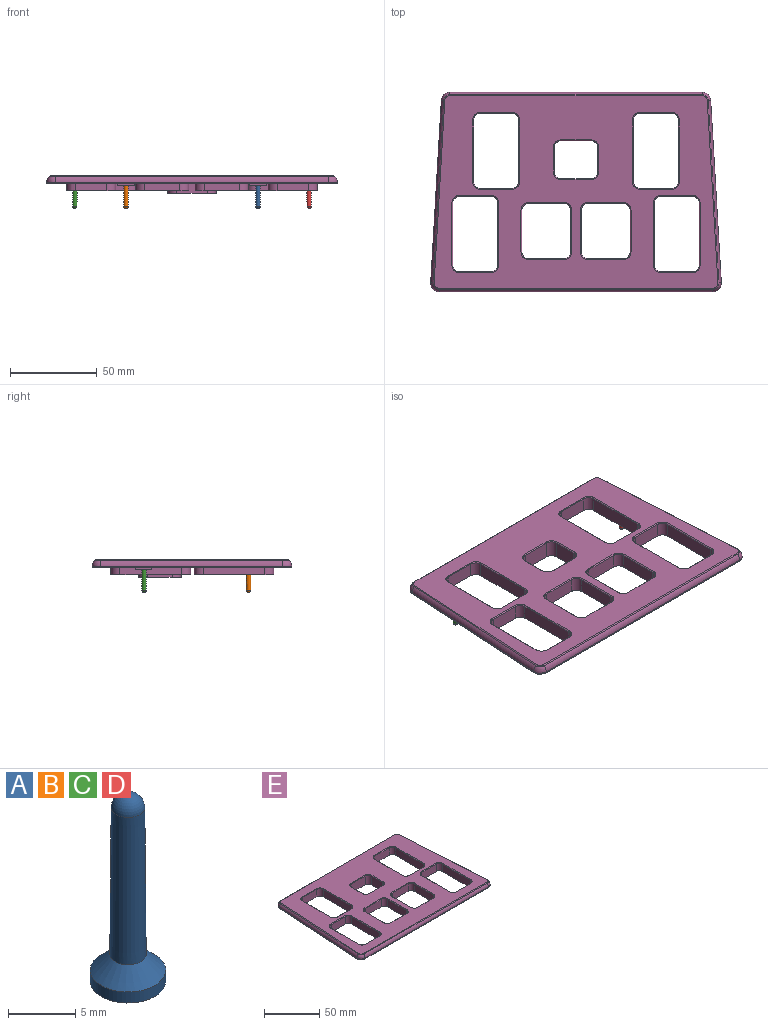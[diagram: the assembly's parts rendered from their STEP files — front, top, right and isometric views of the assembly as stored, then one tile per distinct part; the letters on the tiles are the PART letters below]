
ASSEMBLY  parts=5 mates=4
PART A: 5 faces, bbox 5.6x5.6x17 mm
  f0: plane 5.6x5.6mm, normal (0,0,-1), area 24.6mm2, adj f4
  f1: sphere r=1.25mm, area 9.7mm2, adj f2
  f2: cone r=1.35mm half-angle=0.4deg, axis (0,0,-1), area 108.7mm2, adj f1,f3
  f3: cone r=2.8mm half-angle=45deg, axis (0,0,-1), area 26.7mm2, adj f2,f4
  f4: cylinder r=2.8mm len=5.6mm, axis (0,0,-1), area 17.6mm2, adj f0,f3
PART B: same geometry as A
PART C: same geometry as A
PART D: same geometry as A
PART E: 302 faces, bbox 167.4x115x10.2 mm
  f0: plane 5.45x1.2mm, normal (-1,0,0), area 3.9mm2, adj f7,f10,f181,f219,f299,f301
  f1: plane 5.45x1.2mm, normal (1,0,0), area 3.9mm2, adj f7,f8,f181,f215,f297,f298
  f2: plane 5.45x1.2mm, normal (1,0,0), area 3.9mm2, adj f183,f184,f189,f210,f294,f295
  f3: plane 5.45x1.2mm, normal (1,0,0), area 3.9mm2, adj f176,f177,f178,f191,f287,f289
  f4: plane 5.45x1.2mm, normal (-1,0,0), area 3.9mm2, adj f12,f13,f170,f198,f282,f283
  f5: plane 5.45x1.2mm, normal (1,0,0), area 3.9mm2, adj f11,f12,f170,f203,f278,f280
  f6: plane 162.6x110.2mm, normal (0,0,-1), area 8755.4mm2, adj f8,f9,f10,f11,f13,f80,f81,f82
  f7: plane 2.9x1.2mm, normal (0,1,0), area 3.5mm2, adj f0,f1,f181,f214
  f8: plane 3.9x2.6mm, normal (0,1,0), area 8.5mm2, adj f1,f6,f179,f181,f215,f216,f296,f297
  f9: plane 10x2.6mm, normal (0,-1,0), area 20mm2, adj f6,f179,f180,f181,f214,f215,f216,f218
  f10: plane 3.9x2.6mm, normal (0,1,0), area 8.5mm2, adj f0,f6,f180,f181,f218,f219,f299,f300
  f11: plane 3.9x2.6mm, normal (0,-1,0), area 8.5mm2, adj f5,f6,f167,f170,f202,f203,f278,f279
  f12: plane 2.9x1.2mm, normal (0,-1,0), area 3.5mm2, adj f4,f5,f170,f199
  f13: plane 3.9x2.6mm, normal (0,-1,0), area 8.5mm2, adj f4,f6,f168,f170,f198,f200,f281,f282
  f14: plane 167.4x115mm, normal (0,0,-1), area 1288.3mm2, adj f15,f16,f17,f46,f76,f77,f78,f79
  f15: plane 105x6.12mm, normal (-1,0.06,0), area 76.7mm2, adj f14,f76,f79,f155
  f16: plane 157.4x0.73mm, normal (0,-1,0), area 114.7mm2, adj f14,f76,f77,f158
  f17: plane 105x6.12mm, normal (1,0.06,0), area 76.7mm2, adj f14,f77,f78,f154
  f18: plane 14x9.7mm, normal (1,0,0), area 135.8mm2, adj f72,f75,f142,f257
  f19: plane 17.3x9.7mm, normal (0,-1,0), area 167.8mm2, adj f72,f73,f142,f254
  f20: plane 14x9.7mm, normal (-1,0,0), area 135.8mm2, adj f73,f74,f142,f258
  f21: plane 35.5x8.2mm, normal (1,0,0), area 291.1mm2, adj f68,f71,f88,f265
  f22: plane 18x8.2mm, normal (0,-1,0), area 147.6mm2, adj f68,f69,f88,f262
  f23: plane 35.5x8.2mm, normal (-1,0,0), area 291.1mm2, adj f69,f70,f88,f266
  f24: plane 35.5x8.2mm, normal (1,0,0), area 291.1mm2, adj f64,f67,f124,f233
  f25: plane 18x8.2mm, normal (0,-1,0), area 147.6mm2, adj f64,f65,f124,f230
  f26: plane 35.5x8.2mm, normal (-1,0,0), area 291.1mm2, adj f65,f66,f124,f234
  f27: plane 35.5x8.2mm, normal (1,0,0), area 291.1mm2, adj f60,f63,f97,f273
  f28: plane 18x8.2mm, normal (0,-1,0), area 147.6mm2, adj f60,f61,f97,f270
  f29: plane 35.5x8.2mm, normal (-1,0,0), area 291.1mm2, adj f61,f62,f97,f274
  f30: plane 24x8.2mm, normal (1,0,0), area 196.8mm2, adj f56,f59,f106,f249
  f31: plane 20.2x8.2mm, normal (0,-1,0), area 165.6mm2, adj f56,f57,f106,f246
  f32: plane 24x8.2mm, normal (-1,0,0), area 196.8mm2, adj f57,f58,f106,f250
  f33: plane 24x8.2mm, normal (1,0,0), area 196.8mm2, adj f52,f55,f115,f241
  f34: plane 20.2x8.2mm, normal (0,-1,0), area 165.6mm2, adj f52,f53,f115,f238
  f35: plane 24x8.2mm, normal (-1,0,0), area 196.8mm2, adj f53,f54,f115,f242
  f36: plane 35.5x8.2mm, normal (1,0,0), area 291.1mm2, adj f48,f51,f133,f225
  f37: plane 18x8.2mm, normal (0,-1,0), area 147.6mm2, adj f48,f49,f133,f222
  f38: plane 35.5x8.2mm, normal (-1,0,0), area 291.1mm2, adj f49,f50,f133,f226
  f39: plane 17.3x9.7mm, normal (0,1,0), area 167.8mm2, adj f74,f75,f142,f261
  f40: plane 18x8.2mm, normal (0,1,0), area 147.6mm2, adj f70,f71,f88,f269
  f41: plane 18x8.2mm, normal (0,1,0), area 147.6mm2, adj f66,f67,f124,f237
  f42: plane 18x8.2mm, normal (0,1,0), area 147.6mm2, adj f62,f63,f97,f277
  f43: plane 20.2x8.2mm, normal (0,1,0), area 165.6mm2, adj f58,f59,f106,f253
  f44: plane 20.2x8.2mm, normal (0,1,0), area 165.6mm2, adj f54,f55,f115,f245
  f45: plane 18x8.2mm, normal (0,1,0), area 147.6mm2, adj f50,f51,f133,f229
  f46: plane 145.17x0.73mm, normal (0,1,0), area 105.8mm2, adj f14,f78,f79,f151
  f47: plane 163.4x111mm, normal (0,0,1), area 10235.3mm2, adj f143,f144,f145,f146,f147,f148,f149,f150
  f48: cylinder r=4mm len=8.2mm, axis (0,0,1), area 51.5mm2, adj f36,f37,f133,f223
  f49: cylinder r=4mm len=8.2mm, axis (0,0,-1), area 51.5mm2, adj f37,f38,f133,f224
  f50: cylinder r=4mm len=8.2mm, axis (0,0,1), area 51.5mm2, adj f38,f45,f133,f228
  f51: cylinder r=4mm len=8.2mm, axis (0,0,-1), area 51.5mm2, adj f36,f45,f133,f227
  f52: cylinder r=4mm len=8.2mm, axis (0,0,1), area 51.5mm2, adj f33,f34,f115,f239
  f53: cylinder r=4mm len=8.2mm, axis (0,0,-1), area 51.5mm2, adj f34,f35,f115,f240
  f54: cylinder r=4mm len=8.2mm, axis (0,0,1), area 51.5mm2, adj f35,f44,f115,f244
  f55: cylinder r=4mm len=8.2mm, axis (0,0,-1), area 51.5mm2, adj f33,f44,f115,f243
  f56: cylinder r=4mm len=8.2mm, axis (0,0,1), area 51.5mm2, adj f30,f31,f106,f247
  f57: cylinder r=4mm len=8.2mm, axis (0,0,-1), area 51.5mm2, adj f31,f32,f106,f248
  f58: cylinder r=4mm len=8.2mm, axis (0,0,1), area 51.5mm2, adj f32,f43,f106,f252
  f59: cylinder r=4mm len=8.2mm, axis (0,0,-1), area 51.5mm2, adj f30,f43,f106,f251
  f60: cylinder r=4mm len=8.2mm, axis (0,0,1), area 51.5mm2, adj f27,f28,f97,f271
  f61: cylinder r=4mm len=8.2mm, axis (0,0,-1), area 51.5mm2, adj f28,f29,f97,f272
  f62: cylinder r=4mm len=8.2mm, axis (0,0,1), area 51.5mm2, adj f29,f42,f97,f276
  f63: cylinder r=4mm len=8.2mm, axis (0,0,-1), area 51.5mm2, adj f27,f42,f97,f275
  f64: cylinder r=4mm len=8.2mm, axis (0,0,1), area 51.5mm2, adj f24,f25,f124,f231
  f65: cylinder r=4mm len=8.2mm, axis (0,0,-1), area 51.5mm2, adj f25,f26,f124,f232
  f66: cylinder r=4mm len=8.2mm, axis (0,0,1), area 51.5mm2, adj f26,f41,f124,f236
  f67: cylinder r=4mm len=8.2mm, axis (0,0,-1), area 51.5mm2, adj f24,f41,f124,f235
  f68: cylinder r=4mm len=8.2mm, axis (0,0,1), area 51.5mm2, adj f21,f22,f88,f263
  f69: cylinder r=4mm len=8.2mm, axis (0,0,-1), area 51.5mm2, adj f22,f23,f88,f264
  f70: cylinder r=4mm len=8.2mm, axis (0,0,1), area 51.5mm2, adj f23,f40,f88,f268
  f71: cylinder r=4mm len=8.2mm, axis (0,0,-1), area 51.5mm2, adj f21,f40,f88,f267
  f72: cylinder r=4mm len=9.7mm, axis (0,0,1), area 60.9mm2, adj f18,f19,f142,f255
  f73: cylinder r=4mm len=9.7mm, axis (0,0,-1), area 60.9mm2, adj f19,f20,f142,f256
  f74: cylinder r=4mm len=9.7mm, axis (0,0,1), area 60.9mm2, adj f20,f39,f142,f260
  f75: cylinder r=4mm len=9.7mm, axis (0,0,-1), area 60.9mm2, adj f18,f39,f142,f259
  f76: cylinder r=5mm len=5.29mm, axis (0,0,1), area 5.9mm2, adj f14,f15,f16,f157
  f77: cylinder r=5mm len=5.29mm, axis (0,0,1), area 5.9mm2, adj f14,f16,f17,f156
  f78: cylinder r=5mm len=4.99mm, axis (0,0,1), area 5.5mm2, adj f14,f17,f46,f152
  f79: cylinder r=5mm len=4.99mm, axis (0,0,1), area 5.5mm2, adj f14,f15,f46,f153
  f80: cylinder r=5.2mm len=5.7mm, axis (0,0,1), area 46.6mm2, adj f6,f81,f87,f88
  f81: plane 18x5.7mm, normal (0,1,0), area 102.6mm2, adj f6,f80,f82,f88
  f82: cylinder r=5.2mm len=5.7mm, axis (0,0,1), area 46.6mm2, adj f6,f81,f83,f88
  f83: plane 35.5x5.7mm, normal (-1,0,0), area 202.3mm2, adj f6,f82,f84,f88
  f84: cylinder r=5.2mm len=5.7mm, axis (0,0,1), area 46.6mm2, adj f6,f83,f85,f88
  f85: plane 18x5.7mm, normal (0,-1,0), area 102.6mm2, adj f6,f84,f86,f88
  f86: cylinder r=5.2mm len=5.7mm, axis (0,0,1), area 46.6mm2, adj f6,f85,f87,f88
  f87: plane 35.5x5.7mm, normal (1,0,0), area 202.3mm2, adj f6,f80,f86,f88
  f88: plane 45.9x28.4mm, normal (0,0,-1), area 163.1mm2, adj f21,f22,f23,f40,f68,f69,f70,f71
  f89: cylinder r=5.2mm len=5.7mm, axis (0,0,1), area 46.6mm2, adj f6,f90,f96,f97
  f90: plane 18x5.7mm, normal (0,1,0), area 102.6mm2, adj f6,f89,f91,f97
  f91: cylinder r=5.2mm len=5.7mm, axis (0,0,1), area 46.6mm2, adj f6,f90,f92,f97
  f92: plane 35.5x5.7mm, normal (-1,0,0), area 202.3mm2, adj f6,f91,f93,f97
  f93: cylinder r=5.2mm len=5.7mm, axis (0,0,1), area 46.6mm2, adj f6,f92,f94,f97
  f94: plane 18x5.7mm, normal (0,-1,0), area 102.6mm2, adj f6,f93,f95,f97
  f95: cylinder r=5.2mm len=5.7mm, axis (0,0,1), area 46.6mm2, adj f6,f94,f96,f97
  f96: plane 35.5x5.7mm, normal (1,0,0), area 202.3mm2, adj f6,f89,f95,f97
  f97: plane 45.9x28.4mm, normal (0,0,-1), area 163.1mm2, adj f27,f28,f29,f42,f60,f61,f62,f63
  f98: cylinder r=5.2mm len=5.7mm, axis (0,0,1), area 46.6mm2, adj f6,f99,f105,f106
  f99: plane 20.2x5.7mm, normal (0,1,0), area 115.1mm2, adj f6,f98,f100,f106
  f100: cylinder r=5.2mm len=5.7mm, axis (0,0,1), area 46.6mm2, adj f6,f99,f101,f106
  f101: plane 24x5.7mm, normal (-1,0,0), area 136.8mm2, adj f6,f100,f102,f106
  f102: cylinder r=5.2mm len=5.7mm, axis (0,0,1), area 46.6mm2, adj f6,f101,f103,f106
  f103: plane 20.2x5.7mm, normal (0,-1,0), area 115.1mm2, adj f6,f102,f104,f106
  f104: cylinder r=5.2mm len=5.7mm, axis (0,0,1), area 46.6mm2, adj f6,f103,f105,f106
  f105: plane 24x5.7mm, normal (1,0,0), area 136.8mm2, adj f6,f98,f104,f106
  f106: plane 34.4x30.6mm, normal (0,0,-1), area 140.8mm2, adj f30,f31,f32,f43,f56,f57,f58,f59
  f107: plane 20.2x5.7mm, normal (0,1,0), area 115.1mm2, adj f6,f108,f114,f115
  f108: cylinder r=5.2mm len=5.7mm, axis (0,0,1), area 46.6mm2, adj f6,f107,f109,f115
  f109: plane 24x5.7mm, normal (-1,0,0), area 136.8mm2, adj f6,f108,f110,f115
  f110: cylinder r=5.2mm len=5.7mm, axis (0,0,1), area 46.6mm2, adj f6,f109,f111,f115
  f111: plane 20.2x5.7mm, normal (0,-1,0), area 115.1mm2, adj f6,f110,f112,f115
  f112: cylinder r=5.2mm len=5.7mm, axis (0,0,1), area 46.6mm2, adj f6,f111,f113,f115
  f113: plane 24x5.7mm, normal (1,0,0), area 136.8mm2, adj f6,f112,f114,f115
  f114: cylinder r=5.2mm len=5.7mm, axis (0,0,1), area 46.6mm2, adj f6,f107,f113,f115
  f115: plane 34.4x30.6mm, normal (0,0,-1), area 140.8mm2, adj f33,f34,f35,f44,f52,f53,f54,f55
  f116: cylinder r=5.2mm len=5.7mm, axis (0,0,1), area 46.6mm2, adj f6,f117,f123,f124
  f117: plane 18x5.7mm, normal (0,1,0), area 102.6mm2, adj f6,f116,f118,f124
  f118: cylinder r=5.2mm len=5.7mm, axis (0,0,1), area 46.6mm2, adj f6,f117,f119,f124
  f119: plane 35.5x5.7mm, normal (-1,0,0), area 202.3mm2, adj f6,f118,f120,f124
  f120: cylinder r=5.2mm len=5.7mm, axis (0,0,1), area 46.6mm2, adj f6,f119,f121,f124
  f121: plane 18x5.7mm, normal (0,-1,0), area 102.6mm2, adj f6,f120,f122,f124
  f122: cylinder r=5.2mm len=5.7mm, axis (0,0,1), area 46.6mm2, adj f6,f121,f123,f124
  f123: plane 35.5x5.7mm, normal (1,0,0), area 202.3mm2, adj f6,f116,f122,f124
  f124: plane 45.9x28.4mm, normal (0,0,-1), area 163.1mm2, adj f24,f25,f26,f41,f64,f65,f66,f67
  f125: cylinder r=5.2mm len=5.7mm, axis (0,0,1), area 46.6mm2, adj f6,f126,f132,f133
  f126: plane 18x5.7mm, normal (0,1,0), area 102.6mm2, adj f6,f125,f127,f133
  f127: cylinder r=5.2mm len=5.7mm, axis (0,0,1), area 46.6mm2, adj f6,f126,f128,f133
  f128: plane 35.5x5.7mm, normal (-1,0,0), area 202.3mm2, adj f6,f127,f129,f133
  f129: cylinder r=5.2mm len=5.7mm, axis (0,0,1), area 46.6mm2, adj f6,f128,f130,f133
  f130: plane 18x5.7mm, normal (0,-1,0), area 102.6mm2, adj f6,f129,f131,f133
  f131: cylinder r=5.2mm len=5.7mm, axis (0,0,1), area 46.6mm2, adj f6,f130,f132,f133
  f132: plane 35.5x5.7mm, normal (1,0,0), area 202.3mm2, adj f6,f125,f131,f133
  f133: plane 45.9x28.4mm, normal (0,0,-1), area 163.1mm2, adj f36,f37,f38,f45,f48,f49,f50,f51
  f134: plane 17.3x7.2mm, normal (0,1,0), area 124.6mm2, adj f6,f135,f141,f142
  f135: cylinder r=5.2mm len=7.2mm, axis (0,0,1), area 58.8mm2, adj f6,f134,f136,f142
  f136: plane 14x7.2mm, normal (-1,0,0), area 100.8mm2, adj f6,f135,f137,f142
  f137: cylinder r=5.2mm len=7.2mm, axis (0,0,1), area 58.8mm2, adj f6,f136,f138,f142
  f138: plane 17.3x7.2mm, normal (0,-1,0), area 124.6mm2, adj f6,f137,f139,f142
  f139: cylinder r=5.2mm len=7.2mm, axis (0,0,1), area 58.8mm2, adj f6,f138,f140,f142
  f140: plane 14x7.2mm, normal (1,0,0), area 100.8mm2, adj f6,f139,f141,f142
  f141: cylinder r=5.2mm len=7.2mm, axis (0,0,1), area 58.8mm2, adj f6,f134,f140,f142
  f142: plane 27.7x24.4mm, normal (0,0,-1), area 109.8mm2, adj f18,f19,f20,f39,f72,f73,f74,f75
  f143: plane 157.4x0.54mm, normal (0,-0.71,0.71), area 119.2mm2, adj f47,f144,f145,f158
  f144: cone r=3mm half-angle=45deg, axis (0,0,-1), area 4mm2, adj f47,f143,f146,f156
  f145: cone r=3mm half-angle=45deg, axis (0,0,-1), area 4mm2, adj f47,f143,f147,f157
  f146: plane 105.03x6.65mm, normal (0.71,0.04,0.71), area 79.7mm2, adj f47,f144,f148,f154
  f147: plane 105.03x6.65mm, normal (-0.71,0.04,0.71), area 79.7mm2, adj f47,f145,f149,f155
  f148: cone r=3mm half-angle=45deg, axis (0,0,-1), area 3.7mm2, adj f47,f146,f150,f152
  f149: cone r=3mm half-angle=45deg, axis (0,0,-1), area 3.7mm2, adj f47,f147,f150,f153
  f150: plane 145.17x0.54mm, normal (0,0.71,0.71), area 109.9mm2, adj f47,f148,f149,f151
  f151: cylinder r=5mm len=145.17mm, axis (-1,0,0), area 570.1mm2, adj f46,f150,f152,f153
  f152: sphere r=5mm, area 26.7mm2, adj f78,f148,f151,f154
  f153: sphere r=5mm, area 26.7mm2, adj f79,f149,f151,f155
  f154: cylinder r=5mm len=105.09mm, axis (-0.06,1,0), area 413mm2, adj f17,f146,f152,f156
  f155: cylinder r=5mm len=105.09mm, axis (-0.06,-1,0), area 413mm2, adj f15,f147,f153,f157
  f156: sphere r=5mm, area 28.8mm2, adj f77,f144,f154,f158
  f157: sphere r=5mm, area 28.8mm2, adj f76,f145,f155,f158
  f158: cylinder r=5mm len=157.4mm, axis (1,0,0), area 618.1mm2, adj f16,f143,f156,f157
  f159: plane 145.17x1.8mm, normal (0,-1,0), area 261.3mm2, adj f6,f14,f160,f166
  f160: cylinder r=2.6mm len=2.6mm, axis (0,0,-1), area 7.1mm2, adj f6,f14,f159,f161
  f161: plane 105x6.12mm, normal (-1,-0.06,0), area 189.3mm2, adj f6,f14,f160,f162
  f162: cylinder r=2.6mm len=2.75mm, axis (0,0,-1), area 7.6mm2, adj f6,f14,f161,f163
  f163: plane 157.4x1.8mm, normal (0,1,0), area 283.3mm2, adj f6,f14,f162,f164
  f164: cylinder r=2.6mm len=2.75mm, axis (0,0,-1), area 7.6mm2, adj f6,f14,f163,f165
  f165: plane 105x6.12mm, normal (1,-0.06,0), area 189.3mm2, adj f6,f14,f164,f166
  f166: cylinder r=2.6mm len=2.6mm, axis (0,0,-1), area 7.1mm2, adj f6,f14,f159,f165
  f167: plane 9x2.6mm, normal (-1,0,0), area 23.4mm2, adj f6,f11,f169,f170
  f168: plane 9x2.6mm, normal (1,0,0), area 23.4mm2, adj f6,f13,f169,f170
  f169: plane 10x2.6mm, normal (0,1,0), area 20mm2, adj f6,f167,f168,f170,f198,f199,f200,f202
  f170: plane 10x9mm, normal (0,0,-1), area 74.2mm2, adj f4,f5,f11,f12,f13,f167,f168,f169
  f171: plane 5.45x1.2mm, normal (-1,0,0), area 3.9mm2, adj f172,f177,f178,f190,f285,f286
  f172: plane 3.9x2.6mm, normal (0,-1,0), area 8.5mm2, adj f6,f171,f173,f178,f190,f193,f284,f285
  f173: plane 9x2.6mm, normal (1,0,0), area 23.4mm2, adj f6,f172,f174,f178
  f174: plane 10x2.6mm, normal (0,1,0), area 20mm2, adj f6,f173,f175,f178,f190,f191,f192,f193
  f175: plane 9x2.6mm, normal (-1,0,0), area 23.4mm2, adj f6,f174,f176,f178
  f176: plane 3.9x2.6mm, normal (0,-1,0), area 8.5mm2, adj f3,f6,f175,f178,f191,f195,f287,f288
  f177: plane 2.9x1.2mm, normal (0,-1,0), area 3.5mm2, adj f3,f171,f178,f192
  f178: plane 10x9mm, normal (0,0,-1), area 74.2mm2, adj f3,f171,f172,f173,f174,f175,f176,f177
  f179: plane 9x2.6mm, normal (-1,0,0), area 23.4mm2, adj f6,f8,f9,f181
  f180: plane 9x2.6mm, normal (1,0,0), area 23.4mm2, adj f6,f9,f10,f181
  f181: plane 10x9mm, normal (0,0,-1), area 74.2mm2, adj f0,f1,f7,f8,f9,f10,f179,f180
  f182: plane 5.45x1.2mm, normal (-1,0,0), area 3.9mm2, adj f183,f188,f189,f209,f290,f292
  f183: plane 2.9x1.2mm, normal (0,1,0), area 3.5mm2, adj f2,f182,f189,f206
  f184: plane 3.9x2.6mm, normal (0,1,0), area 8.5mm2, adj f2,f6,f185,f189,f210,f211,f293,f294
  f185: plane 9x2.6mm, normal (-1,0,0), area 23.4mm2, adj f6,f184,f186,f189
  f186: plane 10x2.6mm, normal (0,-1,0), area 20mm2, adj f6,f185,f187,f189,f206,f208,f209,f210
  f187: plane 9x2.6mm, normal (1,0,0), area 23.4mm2, adj f6,f186,f188,f189
  f188: plane 3.9x2.6mm, normal (0,1,0), area 8.5mm2, adj f6,f182,f187,f189,f208,f209,f290,f291
  f189: plane 10x9mm, normal (0,0,-1), area 74.2mm2, adj f2,f182,f183,f184,f185,f186,f187,f188
  f190: plane 9x1.7mm, normal (-0.71,0,0.71), area 18.9mm2, adj f171,f172,f174,f192,f193,f284,f286
  f191: plane 9x1.7mm, normal (0.71,0,0.71), area 18.9mm2, adj f3,f174,f176,f192,f195,f288,f289
  f192: plane 3.55x2.9mm, normal (0,0,1), area 10.3mm2, adj f174,f177,f190,f191
  f193: plane 22x1.05mm, normal (-1,0,0), area 22.4mm2, adj f6,f172,f174,f190,f194,f196,f197
  f194: plane 22x5.6mm, normal (0,0,-1), area 123.2mm2, adj f193,f195,f196,f197
  f195: plane 22x1.05mm, normal (1,0,0), area 22.4mm2, adj f6,f174,f176,f191,f194,f196,f197
  f196: plane 5.6x1mm, normal (0,-1,0), area 5.6mm2, adj f6,f193,f194,f195
  f197: plane 5.6x1mm, normal (0,1,0), area 5.6mm2, adj f6,f193,f194,f195
  f198: plane 9x1.7mm, normal (-0.71,0,0.71), area 18.9mm2, adj f4,f13,f169,f199,f200,f281,f283
  f199: plane 3.55x2.9mm, normal (0,0,1), area 10.3mm2, adj f12,f169,f198,f203
  f200: plane 22x1.05mm, normal (-1,0,0), area 22.4mm2, adj f6,f13,f169,f198,f201,f204,f205
  f201: plane 22x5.6mm, normal (0,0,-1), area 123.2mm2, adj f200,f202,f204,f205
  f202: plane 22x1.05mm, normal (1,0,0), area 22.4mm2, adj f6,f11,f169,f201,f203,f204,f205
  f203: plane 9x1.7mm, normal (0.71,0,0.71), area 18.9mm2, adj f5,f11,f169,f199,f202,f279,f280
  f204: plane 5.6x1mm, normal (0,-1,0), area 5.6mm2, adj f6,f200,f201,f202
  f205: plane 5.6x1mm, normal (0,1,0), area 5.6mm2, adj f6,f200,f201,f202
  f206: plane 3.55x2.9mm, normal (0,0,1), area 10.3mm2, adj f183,f186,f209,f210
  f207: plane 22x5.6mm, normal (0,0,-1), area 123.2mm2, adj f208,f211,f212,f213
  f208: plane 22x1.05mm, normal (-1,0,0), area 22.5mm2, adj f6,f186,f188,f207,f209,f212,f213
  f209: plane 9x1.7mm, normal (-0.71,0,0.71), area 18.9mm2, adj f182,f186,f188,f206,f208,f291,f292
  f210: plane 9x1.7mm, normal (0.71,0,0.71), area 18.9mm2, adj f2,f184,f186,f206,f211,f293,f295
  f211: plane 22x1.05mm, normal (1,0,0), area 22.5mm2, adj f6,f184,f186,f207,f210,f212,f213
  f212: plane 5.6x1mm, normal (0,1,0), area 5.6mm2, adj f6,f207,f208,f211
  f213: plane 5.6x1mm, normal (0,-1,0), area 5.6mm2, adj f6,f207,f208,f211
  f214: plane 3.55x2.9mm, normal (0,0,1), area 10.3mm2, adj f7,f9,f215,f219
  f215: plane 9x1.7mm, normal (0.71,0,0.71), area 18.9mm2, adj f1,f8,f9,f214,f216,f296,f298
  f216: plane 22x1.05mm, normal (1,0,0), area 22.5mm2, adj f6,f8,f9,f215,f217,f220,f221
  f217: plane 22x5.6mm, normal (0,0,-1), area 123.2mm2, adj f216,f218,f220,f221
  f218: plane 22x1.05mm, normal (-1,0,0), area 22.5mm2, adj f6,f9,f10,f217,f219,f220,f221
  f219: plane 9x1.7mm, normal (-0.71,0,0.71), area 18.9mm2, adj f0,f9,f10,f214,f218,f300,f301
  f220: plane 5.6x1mm, normal (0,1,0), area 5.6mm2, adj f6,f216,f217,f218
  f221: plane 5.6x1mm, normal (0,-1,0), area 5.6mm2, adj f6,f216,f217,f218
  f222: plane 18x0.5mm, normal (0,-0.71,0.71), area 12.7mm2, adj f37,f47,f223,f224
  f223: cone r=4.5mm half-angle=45deg, axis (0,0,1), area 4.7mm2, adj f47,f48,f222,f225
  f224: cone r=4.5mm half-angle=45deg, axis (0,0,1), area 4.7mm2, adj f47,f49,f222,f226
  f225: plane 35.5x0.5mm, normal (0.71,0,0.71), area 25.1mm2, adj f36,f47,f223,f227
  f226: plane 35.5x0.5mm, normal (-0.71,0,0.71), area 25.1mm2, adj f38,f47,f224,f228
  f227: cone r=4.5mm half-angle=45deg, axis (0,0,1), area 4.7mm2, adj f47,f51,f225,f229
  f228: cone r=4.5mm half-angle=45deg, axis (0,0,1), area 4.7mm2, adj f47,f50,f226,f229
  f229: plane 18x0.5mm, normal (0,0.71,0.71), area 12.7mm2, adj f45,f47,f227,f228
  f230: plane 18x0.5mm, normal (0,-0.71,0.71), area 12.7mm2, adj f25,f47,f231,f232
  f231: cone r=4.5mm half-angle=45deg, axis (0,0,1), area 4.7mm2, adj f47,f64,f230,f233
  f232: cone r=4.5mm half-angle=45deg, axis (0,0,1), area 4.7mm2, adj f47,f65,f230,f234
  f233: plane 35.5x0.5mm, normal (0.71,0,0.71), area 25.1mm2, adj f24,f47,f231,f235
  f234: plane 35.5x0.5mm, normal (-0.71,0,0.71), area 25.1mm2, adj f26,f47,f232,f236
  f235: cone r=4.5mm half-angle=45deg, axis (0,0,1), area 4.7mm2, adj f47,f67,f233,f237
  f236: cone r=4.5mm half-angle=45deg, axis (0,0,1), area 4.7mm2, adj f47,f66,f234,f237
  f237: plane 18x0.5mm, normal (0,0.71,0.71), area 12.7mm2, adj f41,f47,f235,f236
  f238: plane 20.2x0.5mm, normal (0,-0.71,0.71), area 14.3mm2, adj f34,f47,f239,f240
  f239: cone r=4.5mm half-angle=45deg, axis (0,0,1), area 4.7mm2, adj f47,f52,f238,f241
  f240: cone r=4.5mm half-angle=45deg, axis (0,0,1), area 4.7mm2, adj f47,f53,f238,f242
  f241: plane 24x0.5mm, normal (0.71,0,0.71), area 17mm2, adj f33,f47,f239,f243
  f242: plane 24x0.5mm, normal (-0.71,0,0.71), area 17mm2, adj f35,f47,f240,f244
  f243: cone r=4.5mm half-angle=45deg, axis (0,0,1), area 4.7mm2, adj f47,f55,f241,f245
  f244: cone r=4.5mm half-angle=45deg, axis (0,0,1), area 4.7mm2, adj f47,f54,f242,f245
  f245: plane 20.2x0.5mm, normal (0,0.71,0.71), area 14.3mm2, adj f44,f47,f243,f244
  f246: plane 20.2x0.5mm, normal (0,-0.71,0.71), area 14.3mm2, adj f31,f47,f247,f248
  f247: cone r=4.5mm half-angle=45deg, axis (0,0,1), area 4.7mm2, adj f47,f56,f246,f249
  f248: cone r=4.5mm half-angle=45deg, axis (0,0,1), area 4.7mm2, adj f47,f57,f246,f250
  f249: plane 24x0.5mm, normal (0.71,0,0.71), area 17mm2, adj f30,f47,f247,f251
  f250: plane 24x0.5mm, normal (-0.71,0,0.71), area 17mm2, adj f32,f47,f248,f252
  f251: cone r=4.5mm half-angle=45deg, axis (0,0,1), area 4.7mm2, adj f47,f59,f249,f253
  f252: cone r=4.5mm half-angle=45deg, axis (0,0,1), area 4.7mm2, adj f47,f58,f250,f253
  f253: plane 20.2x0.5mm, normal (0,0.71,0.71), area 14.3mm2, adj f43,f47,f251,f252
  f254: plane 17.3x0.5mm, normal (0,-0.71,0.71), area 12.2mm2, adj f19,f47,f255,f256
  f255: cone r=4.5mm half-angle=45deg, axis (0,0,1), area 4.7mm2, adj f47,f72,f254,f257
  f256: cone r=4.5mm half-angle=45deg, axis (0,0,1), area 4.7mm2, adj f47,f73,f254,f258
  f257: plane 14x0.5mm, normal (0.71,0,0.71), area 9.9mm2, adj f18,f47,f255,f259
  f258: plane 14x0.5mm, normal (-0.71,0,0.71), area 9.9mm2, adj f20,f47,f256,f260
  f259: cone r=4.5mm half-angle=45deg, axis (0,0,1), area 4.7mm2, adj f47,f75,f257,f261
  f260: cone r=4.5mm half-angle=45deg, axis (0,0,1), area 4.7mm2, adj f47,f74,f258,f261
  f261: plane 17.3x0.5mm, normal (0,0.71,0.71), area 12.2mm2, adj f39,f47,f259,f260
  f262: plane 18x0.5mm, normal (0,-0.71,0.71), area 12.7mm2, adj f22,f47,f263,f264
  f263: cone r=4.5mm half-angle=45deg, axis (0,0,1), area 4.7mm2, adj f47,f68,f262,f265
  f264: cone r=4.5mm half-angle=45deg, axis (0,0,1), area 4.7mm2, adj f47,f69,f262,f266
  f265: plane 35.5x0.5mm, normal (0.71,0,0.71), area 25.1mm2, adj f21,f47,f263,f267
  f266: plane 35.5x0.5mm, normal (-0.71,0,0.71), area 25.1mm2, adj f23,f47,f264,f268
  f267: cone r=4.5mm half-angle=45deg, axis (0,0,1), area 4.7mm2, adj f47,f71,f265,f269
  f268: cone r=4.5mm half-angle=45deg, axis (0,0,1), area 4.7mm2, adj f47,f70,f266,f269
  f269: plane 18x0.5mm, normal (0,0.71,0.71), area 12.7mm2, adj f40,f47,f267,f268
  f270: plane 18x0.5mm, normal (0,-0.71,0.71), area 12.7mm2, adj f28,f47,f271,f272
  f271: cone r=4.5mm half-angle=45deg, axis (0,0,1), area 4.7mm2, adj f47,f60,f270,f273
  f272: cone r=4.5mm half-angle=45deg, axis (0,0,1), area 4.7mm2, adj f47,f61,f270,f274
  f273: plane 35.5x0.5mm, normal (0.71,0,0.71), area 25.1mm2, adj f27,f47,f271,f275
  f274: plane 35.5x0.5mm, normal (-0.71,0,0.71), area 25.1mm2, adj f29,f47,f272,f276
  f275: cone r=4.5mm half-angle=45deg, axis (0,0,1), area 4.7mm2, adj f47,f63,f273,f277
  f276: cone r=4.5mm half-angle=45deg, axis (0,0,1), area 4.7mm2, adj f47,f62,f274,f277
  f277: plane 18x0.5mm, normal (0,0.71,0.71), area 12.7mm2, adj f42,f47,f275,f276
  f278: plane 3.5x0.35mm, normal (0,0,-1), area 1.2mm2, adj f5,f11,f279,f280
  f279: plane 3.5x0.4mm, normal (1,0,0), area 1.4mm2, adj f11,f203,f278,f280
  f280: plane 0.75x0.35mm, normal (0,1,0), area 0.2mm2, adj f5,f203,f278,f279
  f281: plane 3.5x0.4mm, normal (-1,0,0), area 1.4mm2, adj f13,f198,f282,f283
  f282: plane 3.5x0.35mm, normal (0,0,-1), area 1.2mm2, adj f4,f13,f281,f283
  f283: plane 0.75x0.35mm, normal (0,1,0), area 0.2mm2, adj f4,f198,f281,f282
  f284: plane 3.5x0.4mm, normal (-1,0,0), area 1.4mm2, adj f172,f190,f285,f286
  f285: plane 3.5x0.35mm, normal (0,0,-1), area 1.2mm2, adj f171,f172,f284,f286
  f286: plane 0.75x0.35mm, normal (0,1,0), area 0.2mm2, adj f171,f190,f284,f285
  f287: plane 3.5x0.35mm, normal (0,0,-1), area 1.2mm2, adj f3,f176,f288,f289
  f288: plane 3.5x0.4mm, normal (1,0,0), area 1.4mm2, adj f176,f191,f287,f289
  f289: plane 0.75x0.35mm, normal (0,1,0), area 0.2mm2, adj f3,f191,f287,f288
  f290: plane 3.5x0.35mm, normal (0,0,-1), area 1.2mm2, adj f182,f188,f291,f292
  f291: plane 3.5x0.4mm, normal (-1,0,0), area 1.4mm2, adj f188,f209,f290,f292
  f292: plane 0.75x0.35mm, normal (0,-1,0), area 0.2mm2, adj f182,f209,f290,f291
  f293: plane 3.5x0.4mm, normal (1,0,0), area 1.4mm2, adj f184,f210,f294,f295
  f294: plane 3.5x0.35mm, normal (0,0,-1), area 1.2mm2, adj f2,f184,f293,f295
  f295: plane 0.75x0.35mm, normal (0,-1,0), area 0.2mm2, adj f2,f210,f293,f294
  f296: plane 3.5x0.4mm, normal (1,0,0), area 1.4mm2, adj f8,f215,f297,f298
  f297: plane 3.5x0.35mm, normal (0,0,-1), area 1.2mm2, adj f1,f8,f296,f298
  f298: plane 0.75x0.35mm, normal (0,-1,0), area 0.2mm2, adj f1,f215,f296,f297
  f299: plane 3.5x0.35mm, normal (0,0,-1), area 1.2mm2, adj f0,f10,f300,f301
  f300: plane 3.5x0.4mm, normal (-1,0,0), area 1.4mm2, adj f10,f219,f299,f301
  f301: plane 0.75x0.35mm, normal (0,-1,0), area 0.2mm2, adj f0,f219,f299,f300
PLACE A rot(axis=(0.93,-0.36,0),180deg) t=(38,24.88,-2)mm
PLACE B rot(axis=(0.81,-0.59,0),180deg) t=(-38,24.88,-2)mm
PLACE C rot(axis=(-0.77,0.64,0),180deg) t=(-67.5,85.1,-2)mm
PLACE D rot(axis=(0.48,0.88,0),180deg) t=(67.5,85.1,-2)mm
PLACE E at identity fixed
MATE pin_slot D.f2 <-> E.f194  axis (0,0,1) through (67.5,85.1,-2)mm
MATE pin_slot A.f2 <-> E.f217  axis (0,0,1) through (38,24.88,-2)mm
MATE pin_slot C.f2 <-> E.f201  axis (0,0,1) through (-67.5,85.1,-2)mm
MATE pin_slot B.f2 <-> E.f207  axis (0,0,1) through (-38,24.88,-2)mm
